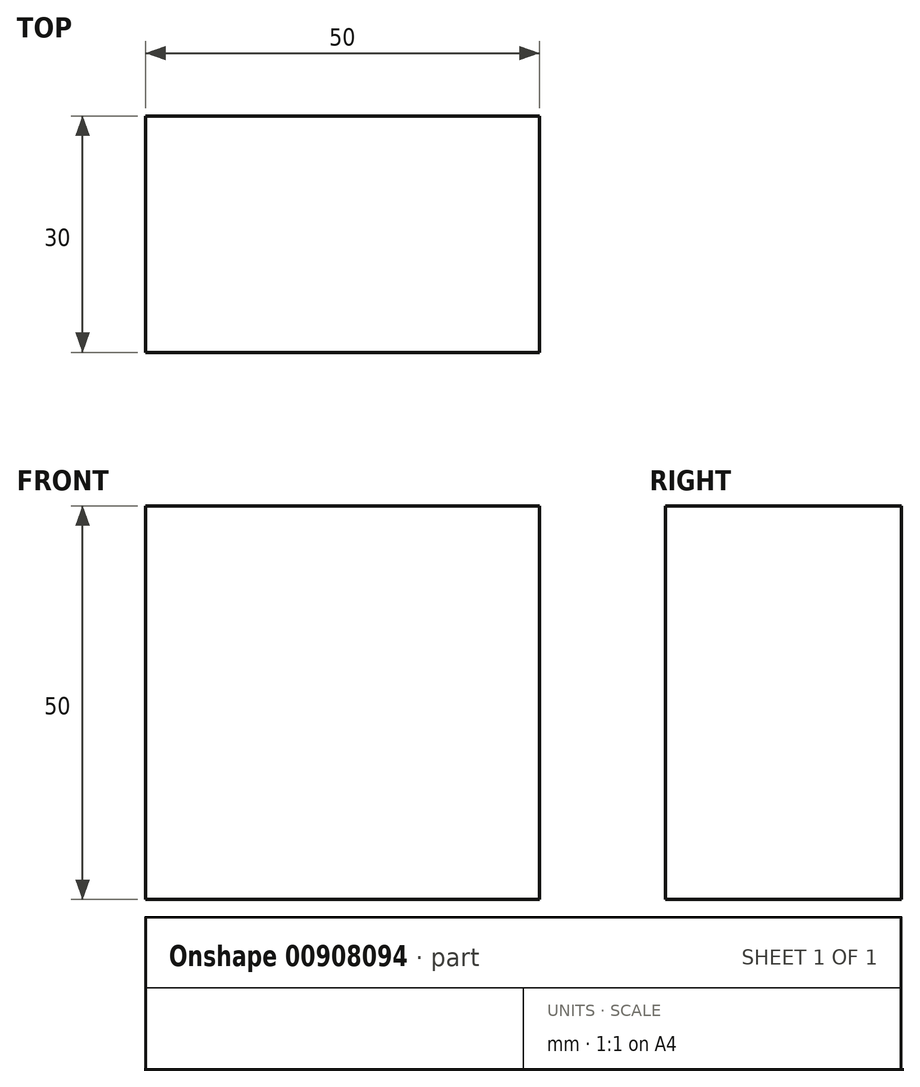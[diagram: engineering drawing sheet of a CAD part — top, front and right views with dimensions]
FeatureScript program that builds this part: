
annotation { "Feature Type Name" : "Feature", "Feature Type Description" : "" }
export const myFeature = defineFeature(function(context is Context, id is Id, definition is map)
    precondition{}
    {
        {
            var Q0;
            Q0=qCreatedBy(makeId("Front.planeOp"),FACE);
            var sketch = newSketch(context, id + "F0", { "sketchPlane" : qUnion([Q0])});
            skLineSegment(sketch, "E0.bottom", {"start": v(-25, -25) * mm, "end": v(25, -25) * mm});
            skLineSegment(sketch, "E0.top", {"start": v(-25, 25) * mm, "end": v(25, 25) * mm});
            skLineSegment(sketch, "E0.left", {"start": v(-25, -25) * mm, "end": v(-25, 25) * mm});
            skLineSegment(sketch, "E0.right", {"start": v(25, -25) * mm, "end": v(25, 25) * mm});
            skPoint(sketch, "E0.middle", {"position": v(0, 0) * mm});
            skSolve(sketch);
        }
        {
            var Q0;
            Q0=qCreatedBy(makeId("Front.planeOp"),FACE);
            cPlane(context, id + "F1", {"entities" : qUnion([Q0]), "cplaneType" : CPlaneType.OFFSET, "offset" : 217.4 * mm, "width" : 150 * mm, "height" : 150 * mm});
        }
        {
            var Q0;
            Q0=makeQuery(id+"F0.imprint","IMPRINT",FACE,{"disambiguationData":[TD([[makeQuery(id+"F0.imprint","IMPRINT",EDGE,{"derivedFrom":sQuery(id+"F0.wireOp",EDGE,"E0.bottom")}),1.0]])]});
            extrude(context, id + "F2", {"entities" : qUnion([Q0]), "depth" : 30 * mm, "offsetDistance" : 25 * mm});
        }
    });
